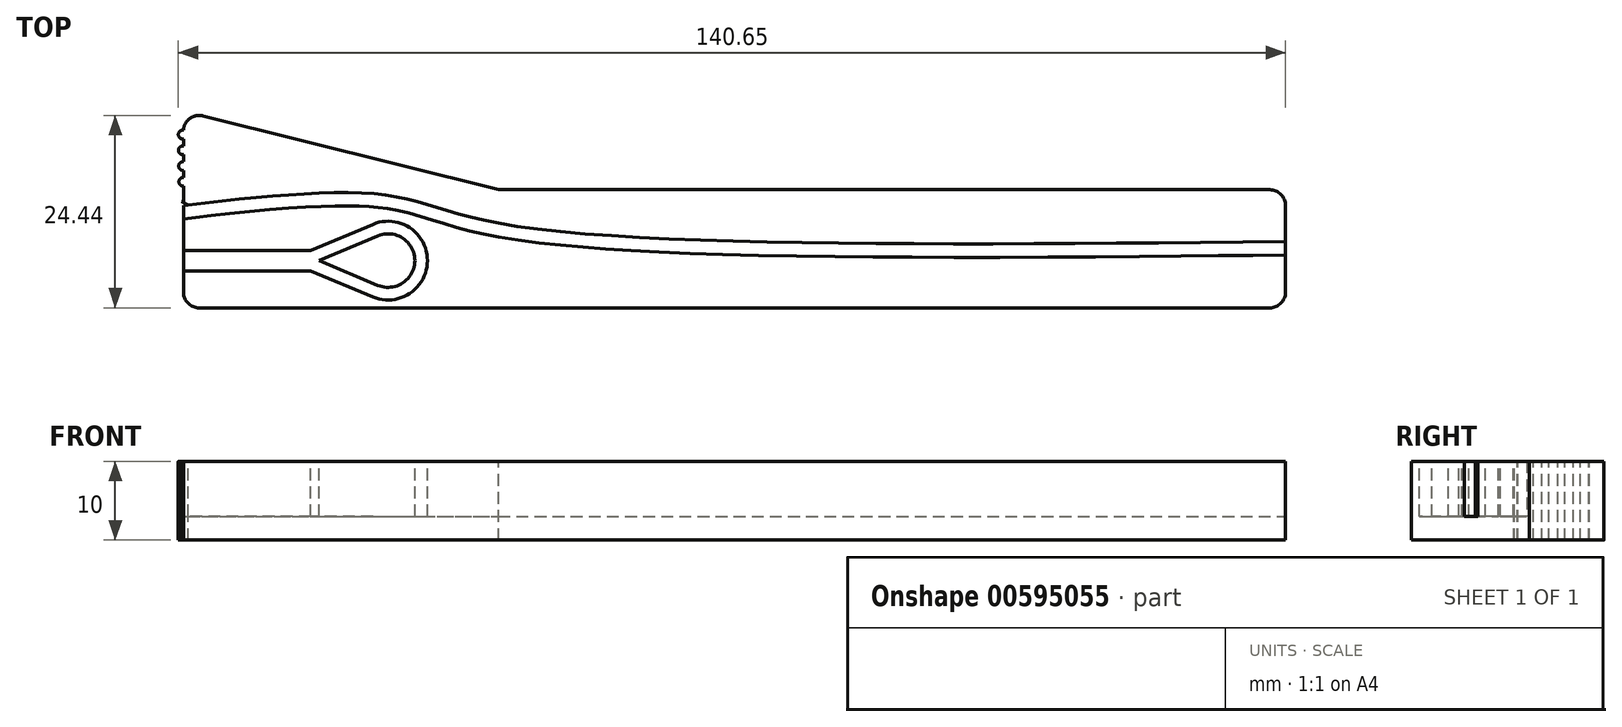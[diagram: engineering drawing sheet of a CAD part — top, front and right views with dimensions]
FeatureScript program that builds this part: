
annotation { "Feature Type Name" : "Feature", "Feature Type Description" : "" }
export const myFeature = defineFeature(function(context is Context, id is Id, definition is map)
    precondition{}
    {
        {
            var Q0;
            Q0=qCreatedBy(makeId("Top.planeOp"),FACE);
            var sketch = newSketch(context, id + "F0", { "sketchPlane" : qUnion([Q0])});
            skLineSegment(sketch, "E0.bottom", {"start": v(0, 7.5) * mm, "end": v(98, 7.5) * mm});
            skLineSegment(sketch, "E0.top", {"start": v(0, -7.5) * mm, "end": v(98, -7.5) * mm});
            skLineSegment(sketch, "E0.left", {"start": v(0, 7.5) * mm, "end": v(0, -7.5) * mm});
            skLineSegment(sketch, "E0.right", {"start": v(100, 5.5) * mm, "end": v(100, -5.5) * mm});
            skLineSegment(sketch, "E1", {"start": v(0, -7.5) * mm, "end": v(-38, -7.5) * mm});
            skLineSegment(sketch, "E2", {"start": v(-40, -5.5) * mm, "end": v(-40, 14.94) * mm});
            skLineSegment(sketch, "E3", {"start": v(-37.51, 16.88) * mm, "end": v(0, 7.5) * mm});
            skPoint(sketch, "E4.visualSharp", {"position": v(-40, 17.5) * mm});
            skArc(sketch, "E4.filletArc", {"start": v(-37.51, 16.88) * mm, "mid": v(-39.23, 16.51) * mm, "end": v(-40, 14.94) * mm});
            skPoint(sketch, "E5.visualSharp", {"position": v(-40, -7.5) * mm});
            skArc(sketch, "E5.filletArc", {"start": v(-40, -5.5) * mm, "mid": v(-39.41, -6.91) * mm, "end": v(-38, -7.5) * mm});
            skPoint(sketch, "E6.visualSharp", {"position": v(100, 7.5) * mm});
            skArc(sketch, "E6.filletArc", {"start": v(100, 5.5) * mm, "mid": v(99.41, 6.91) * mm, "end": v(98, 7.5) * mm});
            skPoint(sketch, "E7.visualSharp", {"position": v(100, -7.5) * mm});
            skArc(sketch, "E7.filletArc", {"start": v(98, -7.5) * mm, "mid": v(99.41, -6.91) * mm, "end": v(100, -5.5) * mm});
            skPoint(sketch, "E8", {"position": v(-14, -1.5) * mm});
            skLineSegment(sketch, "E9.bottom", {"start": v(-18.83, -0.2) * mm, "end": v(-43.6, -0.2) * mm});
            skLineSegment(sketch, "E9.top", {"start": v(-18.83, -2.8) * mm, "end": v(-43.6, -2.8) * mm});
            skLineSegment(sketch, "E9.left", {"start": v(-18.83, -0.2) * mm, "end": v(-18.83, -2.8) * mm});
            skLineSegment(sketch, "E9.right", {"start": v(-43.6, -0.2) * mm, "end": v(-43.6, -2.8) * mm});
            skCircle(sketch, "E10", {"center": v(-14, -1.5) * mm, "radius": 5 * mm});
            skLineSegment(sketch, "E11", {"start": v(-15.93, 3.11) * mm, "end": v(-23.83, -0.2) * mm});
            skLineSegment(sketch, "E12", {"start": v(-15.93, -6.11) * mm, "end": v(-23.83, -2.8) * mm});
            skCircle(sketch, "E13", {"center": v(-14, -1.5) * mm, "radius": 3.4 * mm});
            skCircle(sketch, "E14", {"center": v(-40, 6.51) * mm, "radius": 0.56 * mm});
            skCircle(sketch, "E15.1.0.0", {"center": v(-40.02, 8.51) * mm, "radius": 0.56 * mm});
            skCircle(sketch, "E15.2.0.0", {"center": v(-40.05, 10.5) * mm, "radius": 0.56 * mm});
            skCircle(sketch, "E15.3.0.0", {"center": v(-40.07, 12.5) * mm, "radius": 0.56 * mm});
            skCircle(sketch, "E15.4.0.0", {"center": v(-40.1, 14.5) * mm, "radius": 0.56 * mm});
            skLineSegment(sketch, "E15.direction1", {"start": v(-40, 6.51) * mm, "end": v(-40.02, 8.51) * mm, "construction": true});
            skLineSegment(sketch, "E16", {"start": v(-40.26, 6.02) * mm, "end": v(-39.23, 5.5) * mm});
            skLineSegment(sketch, "E17", {"start": v(-15.32, 1.64) * mm, "end": v(-22.8, -1.5) * mm});
            skLineSegment(sketch, "E18", {"start": v(-22.8, -1.5) * mm, "end": v(-15.32, -4.64) * mm});
            skLineSegment(sketch, "E19.right", {"start": v(100, 0) * mm, "end": v(100, 1.82) * mm});
            skFitSpline(sketch, "E20", {"points": [v(-40.2, 5.5) * mm, v(-14.41, 6.85) * mm, v(0, 3.25) * mm, v(100, 0.91) * mm], "startDerivative": vector(107.73, 12.14) * mm, "endDerivative": vector(235.2, 2.31) * mm});
            skFitSpline(sketch, "E21.0", {"points": [v(-40, 3.81) * mm, v(-37.76, 4.06) * mm, v(-33.27, 4.57) * mm, v(-27.87, 5.08) * mm, v(-23.82, 5.34) * mm, v(-20.95, 5.45) * mm, v(-18.73, 5.45) * mm, v(-17.08, 5.38) * mm, v(-15.9, 5.3) * mm, v(-14.8, 5.19) * mm, v(-13.43, 5) * mm, v(-11.85, 4.66) * mm, v(-10, 4.15) * mm, v(-8.07, 3.55) * mm, v(-5.94, 2.9) * mm, v(-3.52, 2.25) * mm, v(-0.7, 1.62) * mm, v(2.62, 1.08) * mm, v(6.4, 0.62) * mm, v(10.63, 0.22) * mm, v(15.26, -0.11) * mm, v(21.96, -0.48) * mm, v(31.23, -0.8) * mm, v(43.56, -1.01) * mm, v(56.84, -1.08) * mm, v(75.5, -1.03) * mm, v(90.22, -0.89) * mm, v(100.02, -0.79) * mm]});
            skSolve(sketch);
        }
        {
            var Q0;
            Q0=makeQuery(id+"F0.imprint","IMPRINT",FACE,{"disambiguationData":[TD([[makeQuery(id+"F0.imprint","IMPRINT",EDGE,{"derivedFrom":sQuery(id+"F0.wireOp",EDGE,"E0.left")}),-1.0]])]});
            var Q1;
            Q1=makeQuery(id+"F0.imprint","IMPRINT",FACE,{"disambiguationData":[TD([[makeQuery(id+"F0.imprint","IMPRINT",EDGE,{"derivedFrom":sQuery(id+"F0.wireOp",EDGE,"E0.bottom")}),-1.0]])]});
            var Q2;
            {var subQ5=sQuery(id+"F0.wireOp",EDGE,"E9.left");Q2=makeQuery(id+"F0.imprint","IMPRINT",FACE,{"disambiguationData":[TD([[makeQuery(id+"F0.imprint","IMPRINT",EDGE,{"derivedFrom":subQ5}),-1.0]])]});}
            var Q3;
            Q3=makeQuery(id+"F0.imprint","IMPRINT",FACE,{"disambiguationData":[TD([[makeQuery(id+"F0.imprint","IMPRINT",EDGE,{"derivedFrom":sQuery(id+"F0.wireOp",EDGE,"E13")}),1.0]])]});
            var Q4;
            {var subQ2=sQuery(id+"F0.wireOp",EDGE,"E2");var subQ7=sQuery(id+"F0.wireOp",EDGE,"E9.top");var subQ10=makeQuery(id+"F0.imprint","INTERSECT",VERTEX,{"derivedFrom":[subQ2,subQ7]});Q4=makeQuery(id+"F0.imprint","IMPRINT",FACE,{"disambiguationData":[TD([[makeQuery(id+"F0.imprint","IMPRINT",EDGE,{"disambiguationData":[TD([[subQ10,-1.0]])],"derivedFrom":subQ2}),-1.0]])]});}
            var Q5;
            {var subQ3=sQuery(id+"F0.wireOp",EDGE,"E12");Q5=makeQuery(id+"F0.imprint","IMPRINT",FACE,{"disambiguationData":[TD([[makeQuery(id+"F0.imprint","IMPRINT",EDGE,{"derivedFrom":subQ3}),-1.0]])]});}
            var Q6;
            {var subQ3=sQuery(id+"F0.wireOp",EDGE,"E11");Q6=makeQuery(id+"F0.imprint","IMPRINT",FACE,{"disambiguationData":[TD([[makeQuery(id+"F0.imprint","IMPRINT",EDGE,{"derivedFrom":subQ3}),1.0]])]});}
            var Q7;
            {var subQ1=sQuery(id+"F0.wireOp",EDGE,"E9.left");Q7=makeQuery(id+"F0.imprint","IMPRINT",FACE,{"disambiguationData":[TD([[makeQuery(id+"F0.imprint","IMPRINT",EDGE,{"derivedFrom":subQ1}),1.0]])]});}
            var Q8;
            {var subQ0=sQuery(id+"F0.wireOp",EDGE,"E3");Q8=makeQuery(id+"F0.imprint","IMPRINT",FACE,{"disambiguationData":[TD([[makeQuery(id+"F0.imprint","IMPRINT",EDGE,{"derivedFrom":subQ0}),-1.0]])]});}
            var Q9;
            {var subQ3=sQuery(id+"F0.wireOp",EDGE,"E1");Q9=makeQuery(id+"F0.imprint","IMPRINT",FACE,{"disambiguationData":[TD([[makeQuery(id+"F0.imprint","IMPRINT",EDGE,{"derivedFrom":subQ3}),-1.0]])]});}
            var Q10;
            {var subQ1=sQuery(id+"F0.wireOp",EDGE,"E0.top");Q10=makeQuery(id+"F0.imprint","IMPRINT",FACE,{"disambiguationData":[TD([[makeQuery(id+"F0.imprint","IMPRINT",EDGE,{"derivedFrom":subQ1}),1.0]])]});}
            var Q11;
            {var subQ5=sQuery(id+"F0.wireOp",EDGE,"plTAGgz0-8iha-IrbP-ZtMM-bG7OJEWnxcpc.left");Q11=makeQuery(id+"F0.imprint","IMPRINT",FACE,{"disambiguationData":[TD([[makeQuery(id+"F0.imprint","IMPRINT",EDGE,{"derivedFrom":subQ5}),-1.0]])]});}
            var Q12;
            {var subQ0=sQuery(id+"F0.wireOp",EDGE,"E14");var subQ1=sQuery(id+"F0.wireOp",EDGE,"E2");var subQ3=makeQuery(id+"F0.imprint","INTERSECT",VERTEX,{"derivedFrom":[subQ1,subQ0]});Q12=makeQuery(id+"F0.imprint","IMPRINT",FACE,{"disambiguationData":[TD([[makeQuery(id+"F0.imprint","IMPRINT",EDGE,{"disambiguationData":[TD([[subQ3,1.0]])],"derivedFrom":subQ1}),1.0]])]});}
            var Q13;
            {var subQ0=sQuery(id+"F0.wireOp",EDGE,"E14");var subQ1=sQuery(id+"F0.wireOp",EDGE,"E2");var subQ3=makeQuery(id+"F0.imprint","INTERSECT",VERTEX,{"derivedFrom":[subQ1,subQ0]});Q13=makeQuery(id+"F0.imprint","IMPRINT",FACE,{"disambiguationData":[TD([[makeQuery(id+"F0.imprint","IMPRINT",EDGE,{"disambiguationData":[TD([[subQ3,1.0]])],"derivedFrom":subQ1}),-1.0]])]});}
            var Q14;
            {var subQ0=sQuery(id+"F0.wireOp",EDGE,"E15.1.0.0");var subQ1=sQuery(id+"F0.wireOp",EDGE,"E2");var subQ2=makeQuery(id+"F0.imprint","INTERSECT",VERTEX,{"disambiguationData":[OD(0.0)],"derivedFrom":[subQ1,subQ0]});Q14=makeQuery(id+"F0.imprint","IMPRINT",FACE,{"disambiguationData":[TD([[makeQuery(id+"F0.imprint","IMPRINT",EDGE,{"disambiguationData":[TD([[subQ2,-1.0]])],"derivedFrom":subQ1}),1.0]])]});}
            var Q15;
            {var subQ0=sQuery(id+"F0.wireOp",EDGE,"E15.1.0.0");var subQ1=sQuery(id+"F0.wireOp",EDGE,"E2");var subQ2=makeQuery(id+"F0.imprint","INTERSECT",VERTEX,{"disambiguationData":[OD(0.0)],"derivedFrom":[subQ1,subQ0]});Q15=makeQuery(id+"F0.imprint","IMPRINT",FACE,{"disambiguationData":[TD([[makeQuery(id+"F0.imprint","IMPRINT",EDGE,{"disambiguationData":[TD([[subQ2,-1.0]])],"derivedFrom":subQ1}),-1.0]])]});}
            var Q16;
            {var subQ0=sQuery(id+"F0.wireOp",EDGE,"E15.2.0.0");var subQ1=sQuery(id+"F0.wireOp",EDGE,"E2");var subQ2=makeQuery(id+"F0.imprint","INTERSECT",VERTEX,{"disambiguationData":[OD(0.0)],"derivedFrom":[subQ1,subQ0]});Q16=makeQuery(id+"F0.imprint","IMPRINT",FACE,{"disambiguationData":[TD([[makeQuery(id+"F0.imprint","IMPRINT",EDGE,{"disambiguationData":[TD([[subQ2,-1.0]])],"derivedFrom":subQ1}),1.0]])]});}
            var Q17;
            {var subQ0=sQuery(id+"F0.wireOp",EDGE,"E15.3.0.0");var subQ1=sQuery(id+"F0.wireOp",EDGE,"E2");var subQ2=makeQuery(id+"F0.imprint","INTERSECT",VERTEX,{"disambiguationData":[OD(0.0)],"derivedFrom":[subQ1,subQ0]});Q17=makeQuery(id+"F0.imprint","IMPRINT",FACE,{"disambiguationData":[TD([[makeQuery(id+"F0.imprint","IMPRINT",EDGE,{"disambiguationData":[TD([[subQ2,-1.0]])],"derivedFrom":subQ1}),1.0]])]});}
            var Q18;
            {var subQ0=sQuery(id+"F0.wireOp",EDGE,"E4.filletArc");var subQ1=sQuery(id+"F0.wireOp",EDGE,"E2");var subQ2=makeQuery(id+"F0.imprint","INTERSECT",VERTEX,{"derivedFrom":[subQ1,subQ0]});Q18=makeQuery(id+"F0.imprint","IMPRINT",FACE,{"disambiguationData":[TD([[makeQuery(id+"F0.imprint","IMPRINT",EDGE,{"disambiguationData":[TD([[subQ2,1.0]])],"derivedFrom":subQ1}),1.0]])]});}
            var Q19;
            {var subQ0=sQuery(id+"F0.wireOp",EDGE,"E4.filletArc");var subQ1=sQuery(id+"F0.wireOp",EDGE,"E2");var subQ2=makeQuery(id+"F0.imprint","INTERSECT",VERTEX,{"derivedFrom":[subQ1,subQ0]});Q19=makeQuery(id+"F0.imprint","IMPRINT",FACE,{"disambiguationData":[TD([[makeQuery(id+"F0.imprint","IMPRINT",EDGE,{"disambiguationData":[TD([[subQ2,1.0]])],"derivedFrom":subQ1}),-1.0]])]});}
            var Q20;
            {var subQ0=sQuery(id+"F0.wireOp",EDGE,"E15.3.0.0");var subQ1=sQuery(id+"F0.wireOp",EDGE,"E2");var subQ2=makeQuery(id+"F0.imprint","INTERSECT",VERTEX,{"disambiguationData":[OD(0.0)],"derivedFrom":[subQ1,subQ0]});Q20=makeQuery(id+"F0.imprint","IMPRINT",FACE,{"disambiguationData":[TD([[makeQuery(id+"F0.imprint","IMPRINT",EDGE,{"disambiguationData":[TD([[subQ2,-1.0]])],"derivedFrom":subQ1}),-1.0]])]});}
            var Q21;
            {var subQ0=sQuery(id+"F0.wireOp",EDGE,"E15.2.0.0");var subQ1=sQuery(id+"F0.wireOp",EDGE,"E2");var subQ2=makeQuery(id+"F0.imprint","INTERSECT",VERTEX,{"disambiguationData":[OD(0.0)],"derivedFrom":[subQ1,subQ0]});Q21=makeQuery(id+"F0.imprint","IMPRINT",FACE,{"disambiguationData":[TD([[makeQuery(id+"F0.imprint","IMPRINT",EDGE,{"disambiguationData":[TD([[subQ2,-1.0]])],"derivedFrom":subQ1}),-1.0]])]});}
            var Q22;
            {var subQ0=sQuery(id+"F0.wireOp",EDGE,"plTAGgz0-8iha-IrbP-ZtMM-bG7OJEWnxcpc.bottom");var subQ3=sQuery(id+"F0.wireOp",EDGE,"E16");var subQ5=makeQuery(id+"F0.imprint","INTERSECT",VERTEX,{"derivedFrom":[subQ0,subQ3]});Q22=makeQuery(id+"F0.imprint","IMPRINT",FACE,{"disambiguationData":[TD([[makeQuery(id+"F0.imprint","IMPRINT",EDGE,{"disambiguationData":[TD([[subQ5,1.0]])],"derivedFrom":subQ3}),-1.0]])]});}
            var Q23;
            {var subQ0=sQuery(id+"F0.wireOp",EDGE,"E18");var subQ1=sQuery(id+"F0.wireOp",EDGE,"E17");var subQ2=makeQuery(id+"F0.imprint","INTERSECT",VERTEX,{"derivedFrom":[subQ1,subQ0]});Q23=makeQuery(id+"F0.imprint","IMPRINT",FACE,{"disambiguationData":[TD([[makeQuery(id+"F0.imprint","IMPRINT",EDGE,{"disambiguationData":[TD([[subQ2,1.0]])],"derivedFrom":subQ1}),1.0]])]});}
            var Q24;
            {var subQ1=sQuery(id+"F0.wireOp",EDGE,"E9.top");var subQ3=sQuery(id+"F0.wireOp",EDGE,"E18");var subQ4=makeQuery(id+"F0.imprint","INTERSECT",VERTEX,{"derivedFrom":[subQ1,subQ3]});Q24=makeQuery(id+"F0.imprint","IMPRINT",FACE,{"disambiguationData":[TD([[makeQuery(id+"F0.imprint","IMPRINT",EDGE,{"disambiguationData":[TD([[subQ4,-1.0]])],"derivedFrom":subQ3}),1.0]])]});}
            var Q25;
            {var subQ1=sQuery(id+"F0.wireOp",EDGE,"E9.bottom");var subQ3=sQuery(id+"F0.wireOp",EDGE,"E17");var subQ4=makeQuery(id+"F0.imprint","INTERSECT",VERTEX,{"derivedFrom":[subQ1,subQ3]});Q25=makeQuery(id+"F0.imprint","IMPRINT",FACE,{"disambiguationData":[TD([[makeQuery(id+"F0.imprint","IMPRINT",EDGE,{"disambiguationData":[TD([[subQ4,1.0]])],"derivedFrom":subQ3}),1.0]])]});}
            var Q26;
            {var subQ5=sQuery(id+"F0.wireOp",EDGE,"E10");var subQ8=makeQuery(id+"F0.imprint","INTERSECT",VERTEX,{"derivedFrom":[subQ5,sQuery(id+"F0.wireOp",EDGE,"E11")]});Q26=makeQuery(id+"F0.imprint","IMPRINT",FACE,{"disambiguationData":[TD([[makeQuery(id+"F0.imprint","IMPRINT",EDGE,{"disambiguationData":[TD([[subQ8,-1.0]])],"derivedFrom":subQ5}),1.0]])]});}
            var Q27;
            {var subQ5=sQuery(id+"F0.wireOp",EDGE,"E21.0");var subQ6=sQuery(id+"F0.wireOp",EDGE,"E0.left");var subQ7=makeQuery(id+"F0.imprint","INTERSECT",VERTEX,{"derivedFrom":[subQ6,subQ5]});Q27=makeQuery(id+"F0.imprint","IMPRINT",FACE,{"disambiguationData":[TD([[makeQuery(id+"F0.imprint","IMPRINT",EDGE,{"disambiguationData":[TD([[subQ7,1.0]])],"derivedFrom":subQ6}),1.0]])]});}
            extrude(context, id + "F1", {"entities" : qUnion([Q0, Q1, Q2, Q3, Q4, Q5, Q6, Q7, Q8, Q9, Q10, Q11, Q12, Q13, Q14, Q15, Q16, Q17, Q18, Q19, Q20, Q21, Q22, Q23, Q24, Q25, Q26, Q27]), "oppositeDirection" : true, "depth" : 10 * mm, "offsetDistance" : 25 * mm});
        }
        {
            var Q0;
            {var subQ0=sQuery(id+"F0.wireOp",EDGE,"plTAGgz0-8iha-IrbP-ZtMM-bG7OJEWnxcpc.bottom");var subQ3=sQuery(id+"F0.wireOp",EDGE,"E16");var subQ5=makeQuery(id+"F0.imprint","INTERSECT",VERTEX,{"derivedFrom":[subQ0,subQ3]});Q0=makeQuery(id+"F0.imprint","IMPRINT",FACE,{"disambiguationData":[TD([[makeQuery(id+"F0.imprint","IMPRINT",EDGE,{"disambiguationData":[TD([[subQ5,1.0]])],"derivedFrom":subQ3}),-1.0]])]});}
            var Q1;
            {var subQ2=sQuery(id+"F0.wireOp",EDGE,"E9.top");var subQ5=sQuery(id+"F0.wireOp",EDGE,"E2");var subQ6=makeQuery(id+"F0.imprint","INTERSECT",VERTEX,{"derivedFrom":[subQ5,subQ2]});Q1=makeQuery(id+"F0.imprint","IMPRINT",FACE,{"disambiguationData":[TD([[makeQuery(id+"F0.imprint","IMPRINT",EDGE,{"disambiguationData":[TD([[subQ6,-1.0]])],"derivedFrom":subQ5}),-1.0]])]});}
            var Q2;
            {var subQ5=sQuery(id+"F0.wireOp",EDGE,"plTAGgz0-8iha-IrbP-ZtMM-bG7OJEWnxcpc.left");Q2=makeQuery(id+"F0.imprint","IMPRINT",FACE,{"disambiguationData":[TD([[makeQuery(id+"F0.imprint","IMPRINT",EDGE,{"derivedFrom":subQ5}),-1.0]])]});}
            var Q3;
            {var subQ3=sQuery(id+"F0.wireOp",EDGE,"E12");Q3=makeQuery(id+"F0.imprint","IMPRINT",FACE,{"disambiguationData":[TD([[makeQuery(id+"F0.imprint","IMPRINT",EDGE,{"derivedFrom":subQ3}),-1.0]])]});}
            var Q4;
            {var subQ3=sQuery(id+"F0.wireOp",EDGE,"E11");Q4=makeQuery(id+"F0.imprint","IMPRINT",FACE,{"disambiguationData":[TD([[makeQuery(id+"F0.imprint","IMPRINT",EDGE,{"derivedFrom":subQ3}),1.0]])]});}
            var Q5;
            {var subQ5=sQuery(id+"F0.wireOp",EDGE,"E10");var subQ8=makeQuery(id+"F0.imprint","INTERSECT",VERTEX,{"derivedFrom":[subQ5,sQuery(id+"F0.wireOp",EDGE,"E11")]});Q5=makeQuery(id+"F0.imprint","IMPRINT",FACE,{"disambiguationData":[TD([[makeQuery(id+"F0.imprint","IMPRINT",EDGE,{"disambiguationData":[TD([[subQ8,-1.0]])],"derivedFrom":subQ5}),1.0]])]});}
            var Q6;
            {var subQ5=sQuery(id+"F0.wireOp",EDGE,"E21.0");var subQ6=sQuery(id+"F0.wireOp",EDGE,"E0.left");var subQ7=makeQuery(id+"F0.imprint","INTERSECT",VERTEX,{"derivedFrom":[subQ6,subQ5]});Q6=makeQuery(id+"F0.imprint","IMPRINT",FACE,{"disambiguationData":[TD([[makeQuery(id+"F0.imprint","IMPRINT",EDGE,{"disambiguationData":[TD([[subQ7,1.0]])],"derivedFrom":subQ6}),1.0]])]});}
            var Q7;
            {var subQ0=sQuery(id+"F0.wireOp",EDGE,"E20");var subQ4=sQuery(id+"F0.wireOp",EDGE,"E0.left");var subQ5=makeQuery(id+"F0.imprint","INTERSECT",VERTEX,{"derivedFrom":[subQ4,subQ0]});Q7=makeQuery(id+"F0.imprint","IMPRINT",FACE,{"disambiguationData":[TD([[makeQuery(id+"F0.imprint","IMPRINT",EDGE,{"disambiguationData":[TD([[subQ5,-1.0]])],"derivedFrom":subQ4}),-1.0]])]});}
            extrude(context, id + "F2", {"entities" : qUnion([Q0, Q1, Q2, Q3, Q4, Q5, Q6, Q7]), "operationType" : NewBodyOperationType.REMOVE, "oppositeDirection" : true, "depth" : 7 * mm, "offsetDistance" : 25 * mm});
        }
    });
